# Revit family: 1Electronics_Community-Point-Source_Biamp_IP8_1122WR
name_source: partatom
category: Communication Devices
units: mm (PartAtom-declared; Revit-internal decimal feet)

## family parameters
Cut with Voids When Loaded = No
Host = Face
Maintain Annotation Orientation = No
OmniClass Number = 23.85.10.11.14.14.14
OmniClass Title = Loudspeakers
Part Type = Normal
Room Calculation Point = No
Round Connector Dimension = Use Diameter
Shared = No

## types (1)
- Please download type catalogue!
    Continuous Power Handling  Nominal Impedance = LF - 69V, 600W @ 8 ohms (2400W peak); HF - 25V, 80W @ 8 ohms (320W peak)
    Default Elevation = 4' - 0"
    Depth = 1' - 5 11/16"
    Description = IP8-1122WR High Power 12-Inch Two-Way Weather-Resistant Installation Loudspeaker
    Environmental = IP55W per IEC 60529
    Equalized Maximum SPL = Peak: 128 dB - Continuous: 122 dB
    Equalized Sensitivity = 1W: 93 dB - 2.83V: 93 dB
    Gril Material = Biamp - Plastic - Black(Grid)
    Height = 2' - 4"
    Housing Material = Biamp - Plastic - Black
    Input Connection = Screw terminal blocks (6-position)
    Manufacturer = Biamp
    Mounting Points = 15
    Operating Environment = Weather-Resistant Outdoor
    Operating Mode = Passive or Biamp with DSP
    Product Documentation Link = https://www.biamp.com
    Product Page URL = https://www.biamp.com
    Product data url = https://www.bimobject.com
    Recommended Amplifiers = LF - 600W - 1200W @ 8 ohms, (69V - 98V); HF - 80W - 160W @ 8 ohms (25V - 36V)
    Shipping Weight = 74.00 lbf
    Transducers = LF 1 x 12 (305mm) neodymium driver, 3 (76mm) voice coil, demodulation ring; HF 1 x 1.4 (36mm) exit compression, 2.6 (66mm) voice coil, demodulation ring, ketone polymer diaphragm, neodymium compression driver
    URL = https://www.biamp.com
    Weight = 65.00 lbf
    Width = 1' - 2 1/2"

## geometry (parser evidence)
native form markers: Blend x2, Sweep x3
no freeform markers — native parametric forms only
